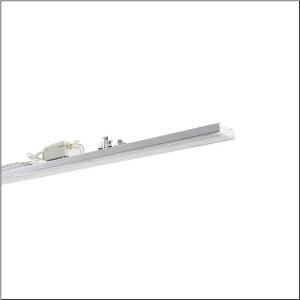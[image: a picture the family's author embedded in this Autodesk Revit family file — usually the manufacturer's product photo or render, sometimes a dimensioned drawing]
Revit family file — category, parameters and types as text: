
# Revit family: licross_r__11_recessed_ho_51tl12dn455md_fc93
name_source: partatom
category: Lighting Fixtures
units: mm (PartAtom-declared; Revit-internal decimal feet)

## family parameters
Cut with Voids When Loaded = No
Host = Face
Light Source = No
Part Type = Normal
Room Calculation Point = No
Round Connector Dimension = Use Diameter
Shared = No

## types (1)
- --- (1 x LED, 900 lm, 5.5 W, 4000K)
    Apparent Load = 6 VA
    CIE Flux Codes = 66 91 98 100 100
    Color Rendering = 80
    Color Temperature = 4000K
    Default Elevation = 1800 mm
    Description = Licross® 11 Recessed HO, luminaire insert, of sheet steel, coil coated, white, length: 1.500mm, width: 66mm, height: 67mm, LED rated luminous flux: 5.960lm, light colour: 840, control gear: DALI 2 (for two DALI lines), with plug, 6-pole, with phase selection, mains connection: 220..240V, AC/DC, 0/50..60Hz, rated input power: 31W, without changeover relay, for emergency light function, for central battery installations according to DIN EN 60598-2-22, halogen-free wiring, primary optical cover: cover, of PMMA, light emission: direct distribution, primary light characteristic: symmetric, protection rating (complete): IP40, insulation class (complete): insulation class I (protective earthing), certification: CE, ENEC, VDE, UKCA, protection symbol: D if used in an environment without relevant dust loads with corresponding accessories, impact resistance: IK06, permissible ambient temperature for indoor applications: -25..+45°C, standard: EN 60598-2-22, corresponds to IFS (International Featured Standards) requirements for safety and quality in the food industry, reducing of maximum allowable ambient temperature of 5°C with ceiling mounting, LABS conformity tested according to VDMA 24364:2018-05, packaging unit: 1 piece
    Height = 58 mm
    Lamp = 1 x LED
    Lamp Light Flux = 900 lm
    Lamp Power = 5.5 W
    Lamp count = 1
    Length = 1500 mm
    Luminous efficacy = 164 lm/W
    Manufacturer = Siteco
    ModVariant = No
    Model = 51TL12DN455MD
    Mounting Place = Ceiling
    Mounting Type = Pendant
    Number of Poles = 1
    OnlyDefault = Yes
    Power Factor = 1
    Product Name = Licross® 11 Recessed HO
    Product group = luminaire insert
    ProductGroupID = 901
    Protection Class = Protection class I
    Protection Degree = IP 40
    RLX_Detail_Level = 1
    RLX_Emergency_Light_Flux = 0 lm
    RLX_Emergency_Type = 0
    RLX_Emergency_Type_DB = No
    RlxData = <blob elided: 24705 chars, md5=ccb7c512>
    Socket = socket
    Standby Power = 0 W
    System Light Flux = 900 lm
    System Power = 6 W
    Type Comments = : DC mode (central or group accumulator) initial emergency light level
    Type Image = l_1296930.jpg
    URL = http://relux.com
    VarID = @adj_082384
    Voltage = 0 V
    Weight = 0.00 kg
    Width = 66 mm

## geometry (parser evidence)
native form markers: Blend x4, Sweep x12
no freeform markers — native parametric forms only
